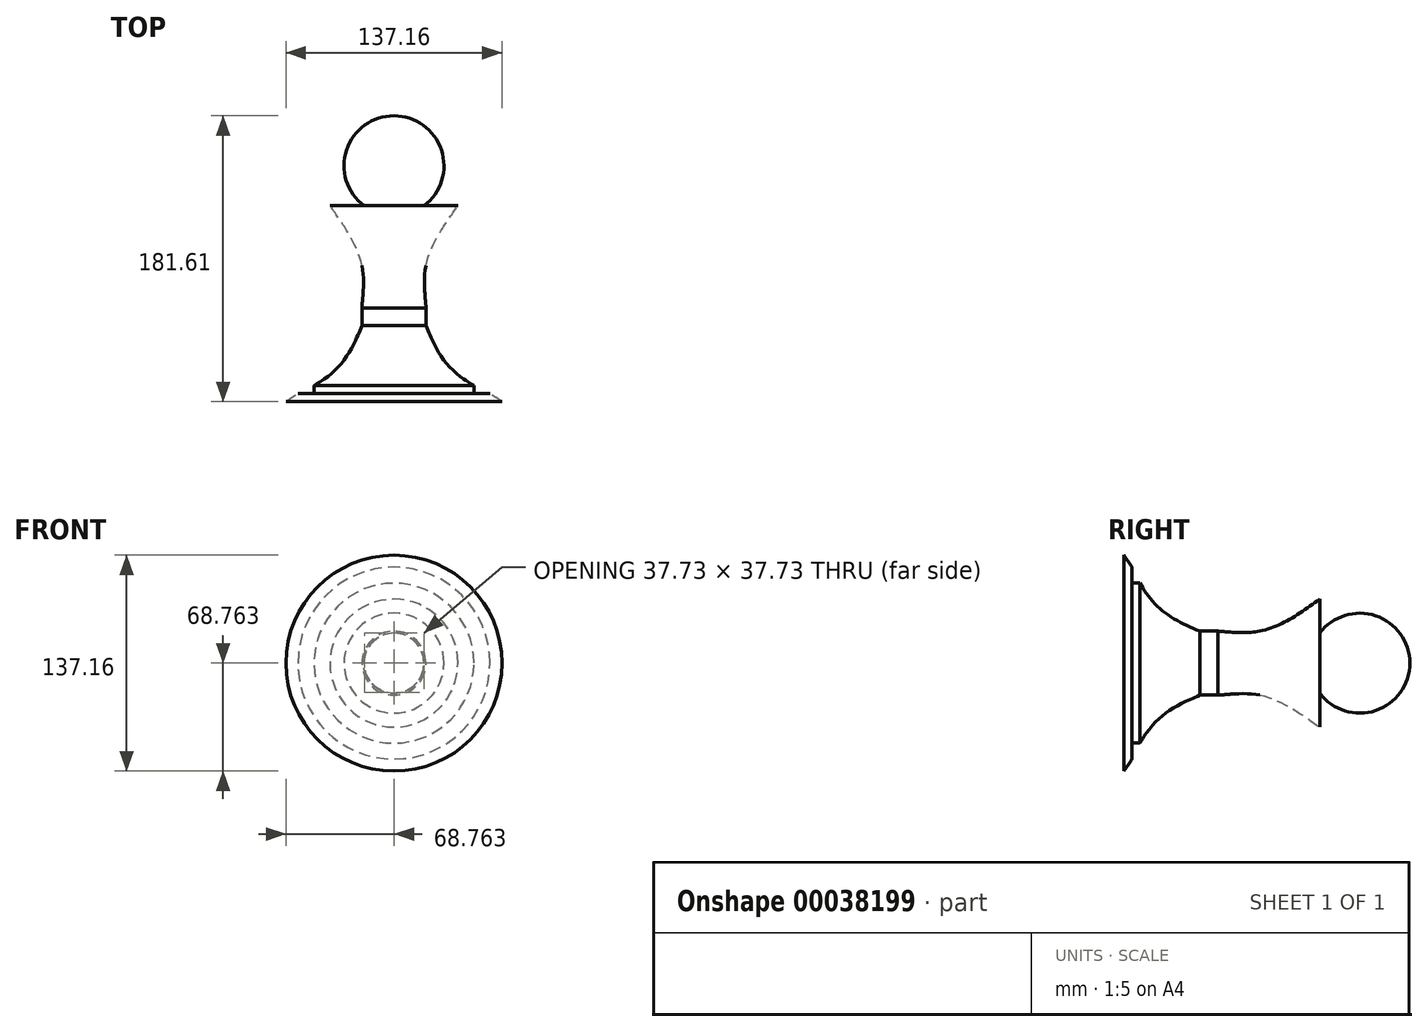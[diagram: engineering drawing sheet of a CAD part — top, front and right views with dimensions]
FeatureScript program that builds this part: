
annotation { "Feature Type Name" : "Feature", "Feature Type Description" : "" }
export const myFeature = defineFeature(function(context is Context, id is Id, definition is map)
    precondition{}
    {
        {
            var Q0;
            Q0=qCreatedBy(makeId("Top.planeOp"),FACE);
            var sketch = newSketch(context, id + "F0", { "sketchPlane" : qUnion([Q0])});
            skLineSegment(sketch, "E0", {"start": v(0, 416.79) * mm, "end": v(406.4, 416.79) * mm});
            skLineSegment(sketch, "E1", {"start": v(19.05, 54.77) * mm, "end": v(40.64, 54.77) * mm});
            skLineSegment(sketch, "E2", {"start": v(20.32, 16.67) * mm, "end": v(20.32, -21.43) * mm});
            skLineSegment(sketch, "E3", {"start": v(0, -69.69) * mm, "end": v(68.58, -69.69) * mm});
            skLineSegment(sketch, "E4", {"start": v(50.8, -64.6) * mm, "end": v(60.96, -64.6) * mm});
            skArc(sketch, "E5", {"start": v(19.05, 54.77) * mm, "mid": v(30.12, 90.21) * mm, "end": v(0, 111.92) * mm});
            skPoint(sketch, "E6.start.orphan", {"position": v(0, 111.92) * mm});
            skFitSpline(sketch, "E7", {"points": [v(40.64, 54.77) * mm, v(20.32, 16.67) * mm, v(20.32, -10.13) * mm, v(19.02, -14.85) * mm, v(3.57, -38.86) * mm], "startDerivative": vector(-73.69, -104.52) * mm, "endDerivative": vector(-68.32, -86.98) * mm});
            skFitSpline(sketch, "E8", {"points": [v(20.32, -21.43) * mm, v(33.12, -45.01) * mm, v(50.8, -59.53) * mm, v(60.96, -64.6) * mm, v(68.58, -69.69) * mm], "startDerivative": vector(34.02, -79.21) * mm, "endDerivative": vector(40.04, -29.23) * mm});
            skLineSegment(sketch, "E9", {"start": v(50.8, -59.53) * mm, "end": v(50.8, -64.6) * mm});
            skFitSpline(sketch, "E10", {"points": [v(60.96, -64.6) * mm, v(68.58, -69.69) * mm, v(68.58, -71.14) * mm], "startDerivative": vector(16.77, -1.4) * mm, "endDerivative": vector(-1.52, -4.82) * mm});
            skPoint(sketch, "E11.start.orphan", {"position": v(0, -21.43) * mm});
            skPoint(sketch, "E12.orphan", {"position": v(0, 16.67) * mm});
            skPoint(sketch, "E13.start.orphan", {"position": v(0, 54.77) * mm});
            skLineSegment(sketch, "E14", {"start": v(0, 111.92) * mm, "end": v(0, -69.69) * mm});
            skSolve(sketch);
        }
        {
            var Q0;
            Q0=makeQuery(id+"F0.imprint","IMPRINT",FACE,{"disambiguationData":[TD([[makeQuery(id+"F0.imprint","IMPRINT",EDGE,{"derivedFrom":sQuery(id+"F0.wireOp",EDGE,"E1")}),-1.0]])]});
            var Q1;
            Q1=sQuery(id+"F0.wireOp",EDGE,"E14");
            revolve(context, id + "F1", {"entities" : qUnion([Q0]), "axis" : qUnion([Q1]), "revolveType" : RevolveType.FULL});
        }
    });
